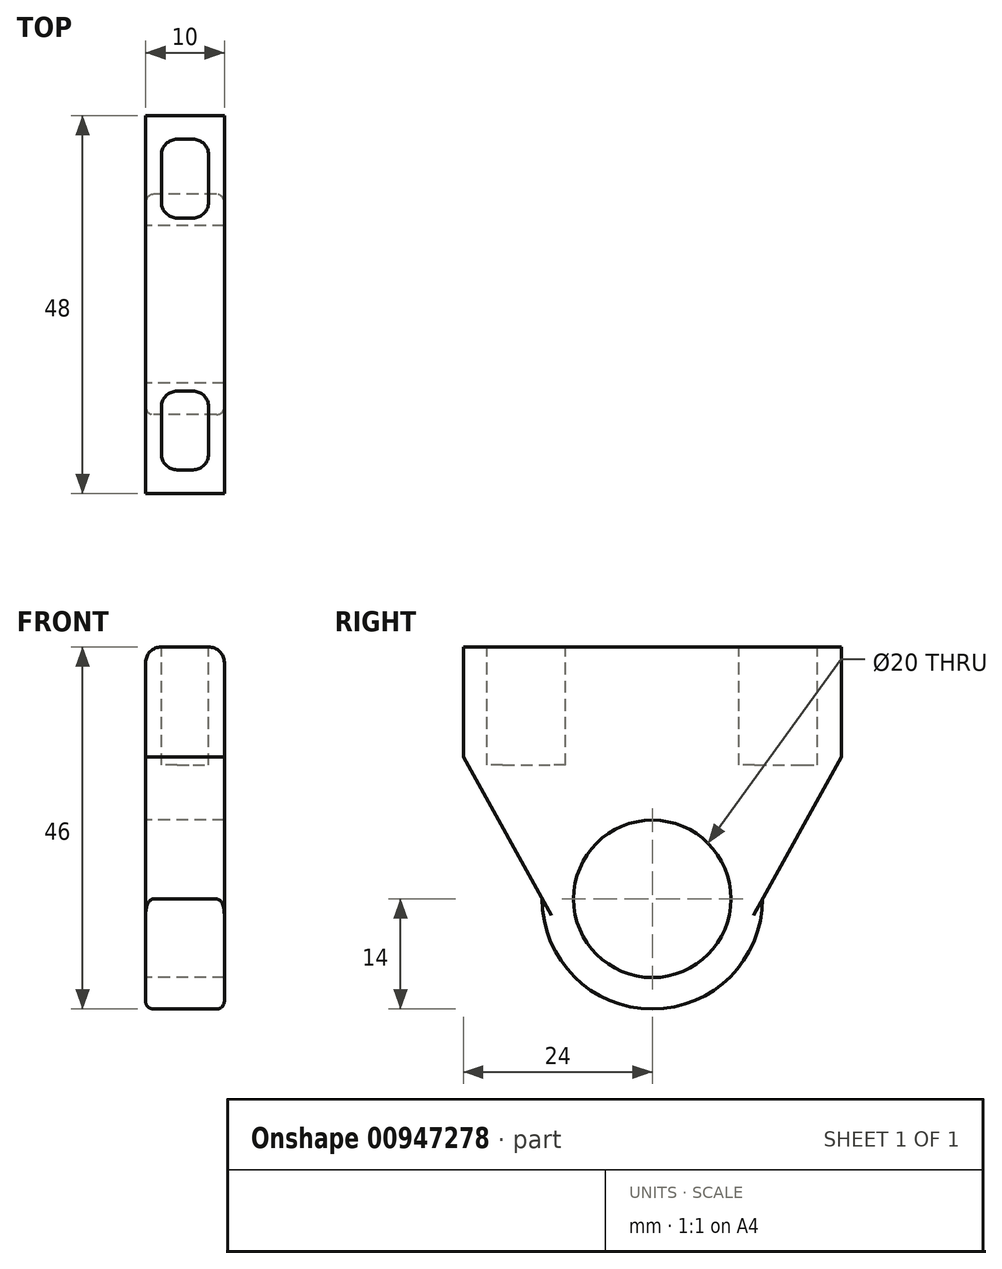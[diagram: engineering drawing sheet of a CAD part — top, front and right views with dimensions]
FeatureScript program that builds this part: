
annotation { "Feature Type Name" : "Feature", "Feature Type Description" : "" }
export const myFeature = defineFeature(function(context is Context, id is Id, definition is map)
    precondition{}
    {
        {
            var Q0;
            Q0=qCreatedBy(makeId("Right.planeOp"),FACE);
            var sketch = newSketch(context, id + "F0", { "sketchPlane" : qUnion([Q0])});
            skCircle(sketch, "E0", {"center": v(0, 0) * mm, "radius": 10 * mm});
            skLineSegment(sketch, "E1.top", {"start": v(-24, 32) * mm, "end": v(24, 32) * mm});
            skLineSegment(sketch, "E1.left", {"start": v(-24, 18) * mm, "end": v(-24, 32) * mm});
            skLineSegment(sketch, "E1.right", {"start": v(24, 18) * mm, "end": v(24, 32) * mm});
            skLineSegment(sketch, "E2", {"start": v(-24, 18) * mm, "end": v(-14, 0) * mm});
            skLineSegment(sketch, "E3", {"start": v(14, 0) * mm, "end": v(24, 18) * mm});
            skArc(sketch, "E4", {"start": v(-14, 0) * mm, "mid": v(0, -14) * mm, "end": v(14, 0) * mm});
            skSolve(sketch);
        }
        {
            var Q0;
            Q0=makeQuery(id+"F0.imprint","IMPRINT",FACE,{"disambiguationData":[TD([[makeQuery(id+"F0.imprint","IMPRINT",EDGE,{"derivedFrom":sQuery(id+"F0.wireOp",EDGE,"E0")}),-1.0]])]});
            extrude(context, id + "F1", {"entities" : qUnion([Q0]), "depth" : 10 * mm, "offsetDistance" : 25 * mm});
        }
        {
            var Q0;
            Q0=makeQuery(id+"F1.opExtrude","CAP_EDGE",EDGE,{"disambiguationData":[OSD([sQuery(id+"F0.wireOp",EDGE,"E4")])],"isStart":true});
            var Q1;
            Q1=makeQuery(id+"F1.opExtrude","CAP_EDGE",EDGE,{"disambiguationData":[OSD([sQuery(id+"F0.wireOp",EDGE,"E4")])],"isStart":false});
            fillet(context, id + "F2", {"entities" : qUnion([Q0, Q1]), "tangentPropagation" : true, "radius" : 1 * mm, "defaultsChanged" : false, "vertexSettings" : [], "allowEdgeOverflow" : false});
        }
        {
            var Q0;
            Q0=makeQuery(id+"F1.opExtrude","CAP_EDGE",EDGE,{"disambiguationData":[OSD([sQuery(id+"F0.wireOp",EDGE,"E1.top")])],"isStart":true});
            var Q1;
            Q1=makeQuery(id+"F1.opExtrude","CAP_EDGE",EDGE,{"disambiguationData":[OSD([sQuery(id+"F0.wireOp",EDGE,"E1.top")])],"isStart":false});
            fillet(context, id + "F3", {"entities" : qUnion([Q0, Q1]), "tangentPropagation" : true, "radius" : 2 * mm, "defaultsChanged" : false, "vertexSettings" : [], "allowEdgeOverflow" : false});
        }
        {
            var Q0;
            Q0=makeQuery(id+"F1.opExtrude","SWEPT_FACE",FACE,{"disambiguationData":[OSD([sQuery(id+"F0.wireOp",EDGE,"E1.top")])]});
            var sketch = newSketch(context, id + "F4", { "sketchPlane" : qUnion([Q0])});
            skLineSegment(sketch, "E5.bottom", {"start": v(2, 21) * mm, "end": v(8, 21) * mm});
            skLineSegment(sketch, "E5.top", {"start": v(2, 11) * mm, "end": v(8, 11) * mm});
            skLineSegment(sketch, "E5.left", {"start": v(2, 21) * mm, "end": v(2, 11) * mm});
            skLineSegment(sketch, "E5.right", {"start": v(8, 21) * mm, "end": v(8, 11) * mm});
            skLineSegment(sketch, "E6.bottom", {"start": v(2, -21) * mm, "end": v(8, -21) * mm});
            skLineSegment(sketch, "E6.top", {"start": v(2, -11) * mm, "end": v(8, -11) * mm});
            skLineSegment(sketch, "E6.left", {"start": v(2, -21) * mm, "end": v(2, -11) * mm});
            skLineSegment(sketch, "E6.right", {"start": v(8, -21) * mm, "end": v(8, -11) * mm});
            skSolve(sketch);
        }
        {
            var Q0;
            Q0 = qSketchRegion(id + "F4", true);
            extrude(context, id + "F5", {"entities" : qUnion([Q0]), "operationType" : NewBodyOperationType.REMOVE, "oppositeDirection" : true, "depth" : 15 * mm, "offsetDistance" : 25 * mm});
        }
        {
            var Q0;
            Q0=makeQuery(id+"F5.boolean.opBoolean","COPY",EDGE,{"derivedFrom":makeQuery(id+"F5.opExtrude","SWEPT_EDGE",EDGE,{"disambiguationData":[OSD([sQuery(id+"F0.wireOp",EDGE,"E1.top"),sQuery(id+"F4.wireOp",EDGE,"E5.bottom"),sQuery(id+"F4.wireOp",EDGE,"E5.left")])]})});
            var Q1;
            Q1=makeQuery(id+"F5.boolean.opBoolean","COPY",EDGE,{"derivedFrom":makeQuery(id+"F5.opExtrude","SWEPT_EDGE",EDGE,{"disambiguationData":[OSD([sQuery(id+"F0.wireOp",EDGE,"E1.top"),sQuery(id+"F4.wireOp",EDGE,"E5.bottom"),sQuery(id+"F4.wireOp",EDGE,"E5.right")])]})});
            var Q2;
            Q2=makeQuery(id+"F5.boolean.opBoolean","COPY",EDGE,{"derivedFrom":makeQuery(id+"F5.opExtrude","SWEPT_EDGE",EDGE,{"disambiguationData":[OSD([sQuery(id+"F0.wireOp",EDGE,"E1.top"),sQuery(id+"F4.wireOp",EDGE,"E5.top"),sQuery(id+"F4.wireOp",EDGE,"E5.right")])]})});
            var Q3;
            Q3=makeQuery(id+"F5.boolean.opBoolean","COPY",EDGE,{"derivedFrom":makeQuery(id+"F5.opExtrude","SWEPT_EDGE",EDGE,{"disambiguationData":[OSD([sQuery(id+"F0.wireOp",EDGE,"E1.top"),sQuery(id+"F4.wireOp",EDGE,"E5.top"),sQuery(id+"F4.wireOp",EDGE,"E5.left")])]})});
            var Q4;
            Q4=makeQuery(id+"F5.boolean.opBoolean","COPY",EDGE,{"derivedFrom":makeQuery(id+"F5.opExtrude","SWEPT_EDGE",EDGE,{"disambiguationData":[OSD([sQuery(id+"F0.wireOp",EDGE,"E1.top"),sQuery(id+"F4.wireOp",EDGE,"E6.bottom"),sQuery(id+"F4.wireOp",EDGE,"E6.left")])]})});
            var Q5;
            Q5=makeQuery(id+"F5.boolean.opBoolean","COPY",EDGE,{"derivedFrom":makeQuery(id+"F5.opExtrude","SWEPT_EDGE",EDGE,{"disambiguationData":[OSD([sQuery(id+"F0.wireOp",EDGE,"E1.top"),sQuery(id+"F4.wireOp",EDGE,"E6.bottom"),sQuery(id+"F4.wireOp",EDGE,"E6.right")])]})});
            var Q6;
            Q6=makeQuery(id+"F5.boolean.opBoolean","COPY",EDGE,{"derivedFrom":makeQuery(id+"F5.opExtrude","SWEPT_EDGE",EDGE,{"disambiguationData":[OSD([sQuery(id+"F0.wireOp",EDGE,"E1.top"),sQuery(id+"F4.wireOp",EDGE,"E6.top"),sQuery(id+"F4.wireOp",EDGE,"E6.right")])]})});
            var Q7;
            Q7=makeQuery(id+"F5.boolean.opBoolean","COPY",EDGE,{"derivedFrom":makeQuery(id+"F5.opExtrude","SWEPT_EDGE",EDGE,{"disambiguationData":[OSD([sQuery(id+"F0.wireOp",EDGE,"E1.top"),sQuery(id+"F4.wireOp",EDGE,"E6.top"),sQuery(id+"F4.wireOp",EDGE,"E6.left")])]})});
            fillet(context, id + "F6", {"entities" : qUnion([Q0, Q1, Q2, Q3, Q4, Q5, Q6, Q7]), "tangentPropagation" : true, "radius" : 2 * mm, "defaultsChanged" : false, "vertexSettings" : [], "allowEdgeOverflow" : false});
        }
    });
